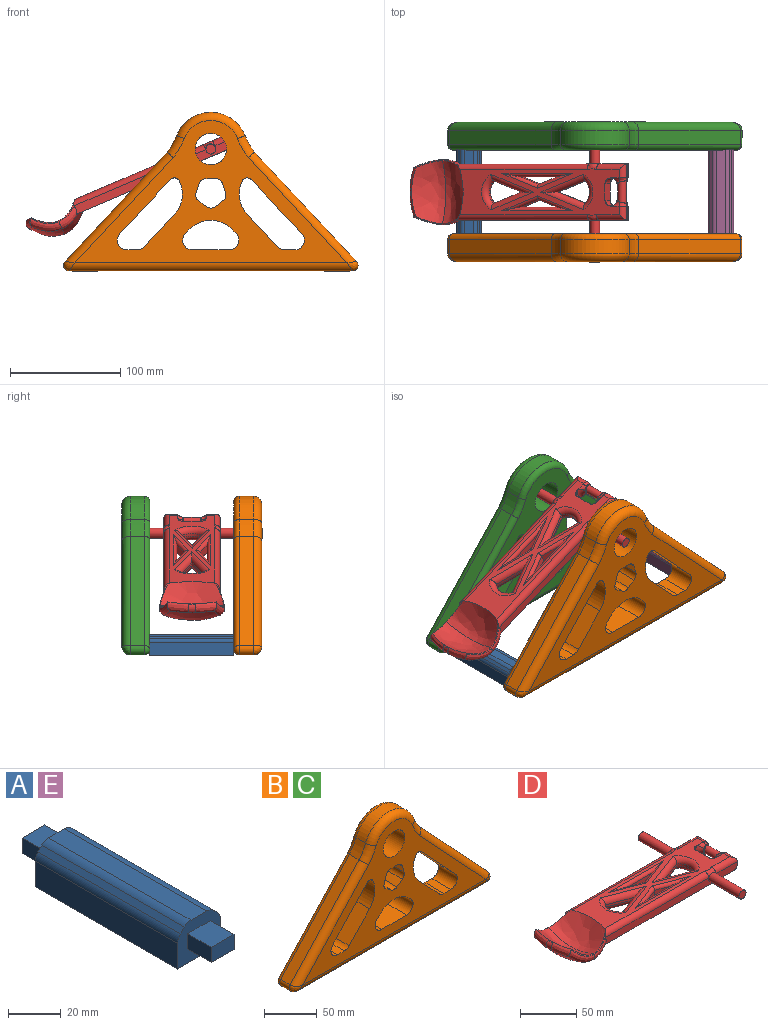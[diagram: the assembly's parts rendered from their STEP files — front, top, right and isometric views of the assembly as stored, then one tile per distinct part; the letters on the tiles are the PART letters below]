
ASSEMBLY  parts=5 mates=4
PART A: 22 faces, bbox 22.9x101.3x19.1 mm
  f0: plane 22.86x19.05mm, normal (0,-1,0), area 322.5mm2, adj f1,f2,f3,f4,f6,f7,f8,f9
  f1: plane 76.2x22.86mm, normal (0,0,-1), area 1741.9mm2, adj f0,f2,f4,f5
  f2: plane 76.2x11.87mm, normal (1,0,0), area 904.2mm2, adj f0,f1,f5,f8
  f3: plane 76.2x8.49mm, normal (0,0,1), area 647.1mm2, adj f0,f5,f9,f10
  f4: plane 76.2x11.87mm, normal (-1,0,0), area 904.2mm2, adj f0,f1,f5,f11
  f5: plane 22.86x19.05mm, normal (0,1,0), area 322.5mm2, adj f1,f2,f3,f4,f6,f7,f8,f9
  f6: plane 76.2x2.1mm, normal (-0.71,0,0.71), area 226.8mm2, adj f0,f5,f9,f11
  f7: plane 76.2x2.1mm, normal (0.71,0,0.71), area 226.8mm2, adj f0,f5,f8,f10
  f8: cylinder r=5.08mm len=76.2mm, axis (0,1,0), area 304mm2, adj f0,f2,f5,f7
  f9: cylinder r=5.08mm len=76.2mm, axis (0,1,0), area 304mm2, adj f0,f3,f5,f6
  f10: cylinder r=5.08mm len=76.2mm, axis (0,1,0), area 304mm2, adj f0,f3,f5,f7
  f11: cylinder r=5.08mm len=76.2mm, axis (0,-1,0), area 304mm2, adj f0,f4,f5,f6
  f12: plane 12.7x7.02mm, normal (1,0,0), area 89.2mm2, adj f0,f13,f15,f21
  f13: plane 12.7x12.1mm, normal (0,0,-1), area 153.7mm2, adj f0,f12,f14,f21
  f14: plane 12.7x7.02mm, normal (-1,0,0), area 89.2mm2, adj f0,f13,f15,f21
  f15: plane 12.7x12.1mm, normal (0,0,1), area 153.7mm2, adj f0,f12,f14,f21
  f16: plane 12.4x7.02mm, normal (1,0,0), area 87mm2, adj f5,f17,f19,f20
  f17: plane 12.1x7.02mm, normal (0,1,0), area 84.9mm2, adj f16,f18,f19,f20
  f18: plane 12.4x7.02mm, normal (-1,0,0), area 87mm2, adj f5,f17,f19,f20
  f19: plane 12.4x12.1mm, normal (0,0,1), area 150mm2, adj f5,f16,f17,f18
  f20: plane 12.4x12.1mm, normal (0,0,-1), area 150mm2, adj f5,f16,f17,f18
  f21: plane 12.1x7.02mm, normal (0,-1,0), area 84.9mm2, adj f12,f13,f14,f15
PART B: 67 faces, bbox 280x26.2x146.5 mm
  f0: plane 256.62x133.63mm, normal (0,1,0), area 11989.8mm2, adj f2,f3,f7,f8,f9,f10,f11,f12
  f1: plane 246.13x129.07mm, normal (0,-1,0), area 10767.5mm2, adj f2,f3,f7,f8,f9,f10,f11,f12
  f2: plane 25.4x9.31mm, normal (0,0,1), area 236.4mm2, adj f0,f1,f23,f25
  f3: cylinder r=14.29mm len=28.58mm, axis (0,1,0), area 2280.2mm2, adj f0,f1
  f4: plane 99.04x92.44mm, normal (0.73,0,0.68), area 1756mm2, adj f16,f37,f56,f57
  f5: plane 99.04x92.44mm, normal (-0.73,0,0.68), area 1756mm2, adj f17,f38,f49,f64
  f6: plane 256.62x12.96mm, normal (0,0,-1), area 3326.2mm2, adj f37,f38,f53,f60
  f7: plane 48.93x45.67mm, normal (-0.73,0,-0.68), area 1700.2mm2, adj f0,f1,f25,f65
  f8: plane 48.93x45.67mm, normal (0.73,0,-0.68), area 1700.2mm2, adj f0,f1,f26,f66
  f9: plane 25.4x9.31mm, normal (0,0,1), area 236.4mm2, adj f0,f1,f24,f26
  f10: plane 29.26x27.31mm, normal (0.73,0,0.68), area 1016.7mm2, adj f0,f1,f19,f23
  f11: plane 29.26x27.31mm, normal (-0.73,0,0.68), area 1016.7mm2, adj f0,f1,f20,f24
  f12: plane 25.4x3.54mm, normal (0.73,0,-0.68), area 123.1mm2, adj f0,f1,f18,f21
  f13: plane 33.42x25.4mm, normal (0,0,1), area 848.9mm2, adj f0,f1,f21,f22
  f14: plane 25.4x3.54mm, normal (-0.73,0,-0.68), area 123.1mm2, adj f0,f1,f18,f22
  f15: cylinder r=33.34mm len=62.04mm, axis (0,1,0), area 1033.4mm2, adj f16,f17,f52,f61
  f16: cylinder r=61.32mm len=15.07mm, axis (0,-1,0), area 225.4mm2, adj f4,f15,f54,f59
  f17: cylinder r=61.32mm len=15.07mm, axis (0,1,0), area 225.4mm2, adj f5,f15,f50,f63
  f18: cylinder r=27.09mm len=39.61mm, axis (0,1,0), area 1128.2mm2, adj f0,f1,f12,f14
  f19: cylinder r=27.09mm len=30.38mm, axis (0,1,0), area 829.5mm2, adj f0,f1,f10,f65
  f20: cylinder r=27.09mm len=30.38mm, axis (0,1,0), area 829.5mm2, adj f0,f1,f11,f66
  f21: cylinder r=8.75mm len=25.4mm, axis (0,-1,0), area 516.1mm2, adj f0,f1,f12,f13
  f22: cylinder r=8.75mm len=25.4mm, axis (0,-1,0), area 516.1mm2, adj f0,f1,f13,f14
  f23: cylinder r=8.75mm len=25.4mm, axis (0,-1,0), area 182.3mm2, adj f0,f1,f2,f10
  f24: cylinder r=8.75mm len=25.4mm, axis (0,1,0), area 182.3mm2, adj f0,f1,f9,f11
  f25: cylinder r=8.75mm len=25.4mm, axis (0,1,0), area 516.1mm2, adj f0,f1,f2,f7
  f26: cylinder r=8.75mm len=25.4mm, axis (0,1,0), area 516.1mm2, adj f0,f1,f8,f9
  f27: plane 25.4x7.21mm, normal (0.59,0,0.81), area 226.4mm2, adj f0,f1,f33,f34
  f28: plane 25.4x7.21mm, normal (-0.59,0,0.81), area 226.4mm2, adj f0,f1,f34,f36
  f29: plane 25.4x8.48mm, normal (-0.95,0,-0.31), area 226.4mm2, adj f0,f1,f35,f36
  f30: plane 25.4x8.91mm, normal (0,0,-1), area 226.4mm2, adj f0,f1,f32,f35
  f31: plane 25.4x8.48mm, normal (0.95,0,-0.31), area 226.4mm2, adj f0,f1,f32,f33
  f32: cylinder r=6.46mm len=25.4mm, axis (0,1,0), area 206.1mm2, adj f0,f1,f30,f31
  f33: cylinder r=6.46mm len=25.4mm, axis (0,1,0), area 206.1mm2, adj f0,f1,f27,f31
  f34: cylinder r=6.46mm len=25.4mm, axis (0,1,0), area 206.1mm2, adj f0,f1,f27,f28
  f35: cylinder r=6.46mm len=25.4mm, axis (0,1,0), area 206.1mm2, adj f0,f1,f29,f30
  f36: cylinder r=6.46mm len=25.4mm, axis (0,1,0), area 206.1mm2, adj f0,f1,f28,f29
  f37: cylinder r=5.08mm len=12.96mm, axis (0,-1,0), area 152.9mm2, adj f4,f6,f55,f58
  f38: cylinder r=5.08mm len=12.96mm, axis (0,-1,0), area 152.9mm2, adj f5,f6,f51,f62
  f39: plane 12.7x12.7mm, normal (0,0,-1), area 161.3mm2, adj f0,f40,f42,f43,f64
  f40: plane 12.7x7.62mm, normal (-1,0,0), area 96.8mm2, adj f0,f39,f41,f43
  f41: plane 12.7x12.7mm, normal (0,0,1), area 161.3mm2, adj f0,f40,f42,f43
  f42: plane 12.7x7.62mm, normal (1,0,0), area 96.8mm2, adj f0,f39,f41,f43,f64
  f43: plane 12.7x7.62mm, normal (0,1,0), area 96.8mm2, adj f39,f40,f41,f42
  f44: plane 12.7x7.62mm, normal (1,0,0), area 96.8mm2, adj f0,f45,f47,f48
  f45: plane 12.7x12.7mm, normal (0,0,-1), area 161.3mm2, adj f0,f44,f46,f48,f57
  f46: plane 12.7x7.62mm, normal (-1,0,0), area 96.8mm2, adj f0,f45,f47,f48,f57
  f47: plane 12.7x12.7mm, normal (0,0,1), area 161.3mm2, adj f0,f44,f46,f48
  f48: plane 12.7x7.62mm, normal (0,1,0), area 96.8mm2, adj f44,f45,f46,f47
  f49: cylinder r=7.36mm len=104.3mm, axis (0.68,0,0.73), area 1545.3mm2, adj f1,f5,f50,f51
  f50: torus R=68.68mm, axis (0,1,0), area 211.2mm2, adj f1,f17,f49,f52
  f51: bspline ~16.93x12.33mm, area 98mm2, adj f38,f49,f53
  f52: torus R=25.98mm, axis (0,1,0), area 847.7mm2, adj f1,f15,f50,f54
  f53: cylinder r=7.36mm len=256.62mm, axis (-1,0,0), area 2922.2mm2, adj f1,f6,f51,f55
  f54: torus R=68.68mm, axis (0,1,0), area 211.2mm2, adj f1,f16,f52,f56
  f55: bspline ~16.93x12.33mm, area 98mm2, adj f37,f53,f56
  f56: cylinder r=7.36mm len=104.3mm, axis (0.68,0,-0.73), area 1545.3mm2, adj f1,f4,f54,f55
  f57: cylinder r=5.08mm len=102.68mm, axis (-0.68,0,0.73), area 1081.7mm2, adj f0,f4,f45,f46,f58,f59
  f58: sphere r=5.08mm, area 59.9mm2, adj f37,f57,f60
  f59: torus R=66.4mm, axis (0,1,0), area 143.9mm2, adj f0,f16,f57,f61
  f60: cylinder r=5.08mm len=256.62mm, axis (1,0,0), area 2047.7mm2, adj f0,f6,f58,f62
  f61: torus R=28.26mm, axis (0,1,0), area 601mm2, adj f0,f15,f59,f63
  f62: sphere r=5.08mm, area 59.9mm2, adj f38,f60,f64
  f63: torus R=66.4mm, axis (0,1,0), area 143.9mm2, adj f0,f17,f61,f64
  f64: cylinder r=5.08mm len=102.68mm, axis (-0.68,0,-0.73), area 1081.7mm2, adj f0,f5,f39,f42,f62,f63
  f65: cylinder r=5.08mm len=25.4mm, axis (0,1,0), area 249.8mm2, adj f0,f1,f7,f19
  f66: cylinder r=5.08mm len=25.4mm, axis (0,1,0), area 249.8mm2, adj f0,f1,f8,f20
PART C: same geometry as B
PART D: 114 faces, bbox 228.8x139.9x39.4 mm
  f0: plane 3.94x1.57mm, normal (-1,0,0), area 2.5mm2, adj f1,f9,f14,f37,f113
  f1: cylinder r=5.08mm len=129.78mm, axis (-1,0,0), area 1022.9mm2, adj f0,f5,f9,f15,f28,f113
  f2: plane 36.48x6.57mm, normal (0,1,0), area 239.6mm2, adj f67,f68,f81,f90
  f3: plane 1.75x1.14mm, normal (0,-1,0), area 0.9mm2, adj f5,f48,f55
  f4: plane 1.75x1.14mm, normal (0,1,0), area 0.9mm2, adj f12,f41,f54
  f5: plane 157.9x44.26mm, normal (0,0,1), area 3253mm2, adj f1,f3,f15,f20,f21,f24,f25,f26
  f6: plane 13.08x2.92mm, normal (1,0,0), area 32.3mm2, adj f10,f22,f27,f45,f51
  f7: offset ~69.48x39.17mm, area 1089.9mm2, adj f12,f17,f31,f37
  f8: plane 41.67x14.21mm, normal (0,0.88,0.47), area 51.5mm2, adj f15,f16,f18,f31,f32,f33
  f9: plane 171.45x15.27mm, normal (0,-1,0), area 1220.4mm2, adj f0,f1,f11,f12,f23,f28,f29,f37
  f10: plane 171.45x15.27mm, normal (0,1,0), area 1220.4mm2, adj f6,f12,f18,f22,f24,f25,f26,f31
  f11: plane 13.08x2.92mm, normal (1,0,0), area 32.3mm2, adj f9,f23,f30,f38,f44
  f12: plane 175.09x63.68mm, normal (0,0,-1), area 4943.5mm2, adj f4,f7,f9,f10,f19,f21,f22,f23
  f13: cone r=41.27mm half-angle=33.7deg, axis (-1,0,0), area 3.4mm2, adj f33,f34,f35
  f14: plane 41.67x14.21mm, normal (0,-0.88,0.47), area 51.5mm2, adj f0,f15,f16,f35,f36,f37
  f15: bspline ~56.78x26.47mm, area 1620.2mm2, adj f1,f5,f8,f14,f16,f24,f112,f113
  f16: bspline ~56.78x26.47mm, area 1566.3mm2, adj f8,f14,f15,f33,f35
  f17: offset ~69.48x39.17mm, area 1534.5mm2, adj f7,f32,f33,f34,f35,f36
  f18: plane 3.94x1.57mm, normal (-1,0,0), area 2.5mm2, adj f8,f10,f24,f31,f112
  f19: plane 1.75x1.14mm, normal (0,-1,0), area 0.9mm2, adj f12,f48,f57
  f20: plane 1.75x1.14mm, normal (0,1,0), area 0.9mm2, adj f5,f41,f52
  f21: plane 15.49x12.7mm, normal (1,0,0), area 194.7mm2, adj f5,f12,f52,f53,f54,f55,f56,f57
  f22: cylinder r=5.08mm len=12.7mm, axis (0,1,0), area 101.3mm2, adj f6,f10,f12,f50
  f23: cylinder r=5.08mm len=12.7mm, axis (0,1,0), area 101.3mm2, adj f9,f11,f12,f43
  f24: cylinder r=5.08mm len=129.78mm, axis (1,0,0), area 1022.9mm2, adj f5,f10,f15,f18,f25,f112
  f25: bspline ~10.61x5.27mm, area 50.7mm2, adj f5,f10,f24,f26
  f26: cylinder r=5.08mm len=27.16mm, axis (1,0,0), area 196.5mm2, adj f5,f10,f25,f27
  f27: cylinder r=5.08mm len=12.7mm, axis (0,-1,0), area 81.1mm2, adj f5,f6,f26,f46
  f28: bspline ~10.61x5.27mm, area 50.7mm2, adj f1,f5,f9,f29
  f29: cylinder r=5.08mm len=27.16mm, axis (-1,0,0), area 196.5mm2, adj f5,f9,f28,f30
  f30: cylinder r=5.08mm len=12.7mm, axis (0,-1,0), area 81.1mm2, adj f5,f11,f29,f39
  f31: bspline ~27.95x15.74mm, area 166.3mm2, adj f7,f8,f10,f12,f18,f32
  f32: bspline ~34.17x21.98mm, area 241.4mm2, adj f8,f17,f31,f33
  f33: bspline ~29.07x10.69mm, area 179.5mm2, adj f8,f13,f16,f17,f32,f34
  f34: torus R=46.13mm, axis (-1,0,0), area 51.9mm2, adj f13,f17,f33,f35
  f35: bspline ~30.88x10.69mm, area 179.5mm2, adj f13,f14,f16,f17,f34,f36
  f36: bspline ~34.17x21.98mm, area 241.4mm2, adj f14,f17,f35,f37
  f37: bspline ~27.95x15.74mm, area 166.3mm2, adj f0,f7,f9,f12,f14,f36
  f38: bspline ~2.25x1.59mm, area 0.4mm2, adj f11,f39,f98
  f39: bspline ~6.12x5.09mm, area 22.5mm2, adj f30,f38,f40,f97
  f40: bspline ~8.34x5.27mm, area 27.5mm2, adj f5,f39,f41,f96
  f41: torus R=10.08mm, axis (0,1,0), area 74.5mm2, adj f4,f20,f40,f42,f53,f95
  f42: bspline ~8.36x5.31mm, area 27.5mm2, adj f12,f41,f43,f94
  f43: bspline ~6x5.46mm, area 22.4mm2, adj f23,f42,f44,f93
  f44: bspline ~2.45x1.72mm, area 0.4mm2, adj f11,f43,f106
  f45: bspline ~2.25x1.59mm, area 0.4mm2, adj f6,f46,f105
  f46: bspline ~6.12x5.09mm, area 22.5mm2, adj f27,f45,f47,f99
  f47: bspline ~8.34x5.27mm, area 27.5mm2, adj f5,f46,f48,f100
  f48: torus R=10.08mm, axis (0,1,0), area 74.5mm2, adj f3,f19,f47,f49,f56,f101
  f49: bspline ~8.36x5.31mm, area 27.5mm2, adj f12,f48,f50,f102
  f50: bspline ~6.01x5.08mm, area 22.4mm2, adj f22,f49,f51,f103
  f51: bspline ~2.45x1.72mm, area 0.4mm2, adj f6,f50,f104
  f52: cylinder r=5.08mm len=5.08mm, axis (0,0,1), area 14mm2, adj f5,f20,f21,f53
  f53: bspline ~10.08x5.32mm, area 66.5mm2, adj f21,f41,f52,f54
  f54: cylinder r=5.08mm len=5.08mm, axis (0,0,1), area 14mm2, adj f4,f12,f21,f53
  f55: cylinder r=5.08mm len=5.08mm, axis (0,0,-1), area 14mm2, adj f3,f5,f21,f56
  f56: bspline ~10.37x5.36mm, area 66.5mm2, adj f21,f48,f55,f57
  f57: cylinder r=5.08mm len=5.08mm, axis (0,0,-1), area 14mm2, adj f12,f19,f21,f56
  f58: cylinder r=13.76mm len=20.8mm, axis (0,0,1), area 59.9mm2, adj f61,f62,f69,f72
  f59: cylinder r=13.76mm len=20.8mm, axis (0,0,1), area 59.9mm2, adj f63,f64,f76,f79
  f60: plane 36.48x6.57mm, normal (0,-1,0), area 239.6mm2, adj f65,f66,f84,f87
  f61: plane 27.25x10.4mm, normal (-0.36,-0.93,0), area 74.1mm2, adj f58,f62,f70,f73
  f62: plane 27.25x10.4mm, normal (-0.36,0.93,0), area 74.1mm2, adj f58,f61,f71,f74
  f63: plane 27.25x10.4mm, normal (0.36,0.93,0), area 74.1mm2, adj f59,f64,f75,f78
  f64: plane 27.25x10.4mm, normal (0.36,-0.93,0), area 74.1mm2, adj f59,f63,f77,f80
  f65: plane 18.24x6.96mm, normal (0.36,0.93,0), area 128.2mm2, adj f60,f66,f86,f89
  f66: plane 18.24x6.96mm, normal (-0.36,0.93,0), area 128.2mm2, adj f60,f65,f85,f88
  f67: plane 18.24x6.96mm, normal (0.36,-0.93,0), area 128.2mm2, adj f2,f68,f83,f92
  f68: plane 18.24x6.96mm, normal (-0.36,-0.93,0), area 128.2mm2, adj f2,f67,f82,f91
  f69: torus R=18.84mm, axis (0,0,1), area 235.7mm2, adj f5,f58,f70,f71
  f70: cylinder r=5.08mm len=44.05mm, axis (0.93,-0.36,0), area 296.8mm2, adj f5,f61,f69,f71
  f71: cylinder r=5.08mm len=44.05mm, axis (0.93,0.36,0), area 296.8mm2, adj f5,f62,f69,f70
  f72: torus R=18.84mm, axis (0,0,1), area 235.7mm2, adj f12,f58,f73,f74
  f73: cylinder r=5.08mm len=44.05mm, axis (-0.93,0.36,0), area 296.8mm2, adj f12,f61,f72,f74
  f74: cylinder r=5.08mm len=44.05mm, axis (-0.93,-0.36,0), area 296.8mm2, adj f12,f62,f72,f73
  f75: cylinder r=5.08mm len=44.05mm, axis (0.93,-0.36,0), area 296.8mm2, adj f5,f63,f76,f77
  f76: torus R=18.84mm, axis (0,0,1), area 235.7mm2, adj f5,f59,f75,f77
  f77: cylinder r=5.08mm len=44.05mm, axis (0.93,0.36,0), area 296.8mm2, adj f5,f64,f75,f76
  f78: cylinder r=5.08mm len=44.05mm, axis (-0.93,0.36,0), area 296.8mm2, adj f12,f63,f79,f80
  f79: torus R=18.84mm, axis (0,0,1), area 235.7mm2, adj f12,f59,f78,f80
  f80: cylinder r=5.08mm len=44.05mm, axis (-0.93,-0.36,0), area 296.8mm2, adj f12,f64,f78,f79
  f81: cylinder r=3.07mm len=69.75mm, axis (-1,0,0), area 255.8mm2, adj f2,f5,f82,f83
  f82: cylinder r=3.07mm len=35.97mm, axis (-0.93,0.36,0), area 126mm2, adj f5,f68,f81,f83
  f83: cylinder r=3.07mm len=35.97mm, axis (0.93,0.36,0), area 126mm2, adj f5,f67,f81,f82
  f84: cylinder r=3.07mm len=69.75mm, axis (1,0,0), area 255.8mm2, adj f5,f60,f85,f86
  f85: cylinder r=3.07mm len=35.97mm, axis (0.93,0.36,0), area 126mm2, adj f5,f66,f84,f86
  f86: cylinder r=3.07mm len=35.97mm, axis (0.93,-0.36,0), area 126mm2, adj f5,f65,f84,f85
  f87: cylinder r=3.07mm len=69.75mm, axis (-1,0,0), area 255.8mm2, adj f12,f60,f88,f89
  f88: cylinder r=3.07mm len=35.97mm, axis (-0.93,-0.36,0), area 126mm2, adj f12,f66,f87,f89
  f89: cylinder r=3.07mm len=35.97mm, axis (-0.93,0.36,0), area 126mm2, adj f12,f65,f87,f88
  f90: cylinder r=3.07mm len=69.75mm, axis (1,0,0), area 255.8mm2, adj f2,f12,f91,f92
  f91: cylinder r=3.07mm len=35.97mm, axis (0.93,-0.36,0), area 126mm2, adj f12,f68,f90,f92
  f92: cylinder r=3.07mm len=35.97mm, axis (-0.93,-0.36,0), area 126mm2, adj f12,f67,f90,f91
  f93: bspline ~5x4.53mm, area 9mm2, adj f43,f94,f106,f107
  f94: bspline ~3.85x2.65mm, area 5.4mm2, adj f42,f93,f95,f107
  f95: plane 6.3x2.1mm, normal (0,1,0), area 7.6mm2, adj f41,f94,f96,f107
  f96: bspline ~3.85x2.65mm, area 5.4mm2, adj f40,f95,f97,f107
  f97: bspline ~5x4.53mm, area 9mm2, adj f39,f96,f98,f107
  f98: bspline ~1.3x0.9mm, area 1.3mm2, adj f38,f97,f106,f107
  f99: bspline ~5x4.53mm, area 9mm2, adj f46,f100,f105,f107
  f100: bspline ~3.85x2.65mm, area 5.4mm2, adj f47,f99,f101,f107
  f101: plane 6.3x2.1mm, normal (0,-1,0), area 7.6mm2, adj f48,f100,f102,f107
  f102: bspline ~3.85x2.65mm, area 5.4mm2, adj f49,f101,f103,f107
  f103: bspline ~5x4.53mm, area 9mm2, adj f50,f102,f104,f107
  f104: bspline ~1.3x0.9mm, area 1.3mm2, adj f51,f103,f105,f107
  f105: bspline ~1.3x0.9mm, area 1.3mm2, adj f45,f99,f104,f107
  f106: bspline ~1.3x0.9mm, area 1.3mm2, adj f44,f93,f98,f107
  f107: cylinder r=3.73mm len=25.4mm, axis (0,-1,0), area 427.7mm2, adj f93,f94,f95,f96,f97,f98,f99,f100
  f108: cylinder r=4.46mm len=38.1mm, axis (0,1,0), area 1068.3mm2, adj f10,f110
  f109: cylinder r=4.46mm len=38.1mm, axis (0,1,0), area 1068.3mm2, adj f9,f111
  f110: plane 8.93x8.93mm, normal (0,1,0), area 62.6mm2, adj f108
  f111: plane 8.93x8.93mm, normal (0,-1,0), area 62.6mm2, adj f109
  f112: extruded ~3.68x3.06mm, area 2.7mm2, adj f15,f18,f24
  f113: extruded ~3.68x3.06mm, area 2.7mm2, adj f0,f1,f15
PART E: same geometry as A
PLACE A t=(-183.55,-13.21,39.08)mm
PLACE B t=(-69.25,-102.11,29.56)mm fixed
PLACE C rot(axis=(0,0,1),180deg) t=(-69.25,-26.21,29.56)mm
PLACE D rot(axis=(0,-1,0),23.1deg) t=(-116.4,-64.31,112.99)mm
PLACE E t=(45.05,-13.21,39.08)mm
MATE fastened A.f17 <-> C.f48  axis (0,1,0) through (-183.55,-13.51,39.08)mm
MATE fastened A.f21 <-> B.f43  axis (0,-1,0) through (-183.55,-114.81,39.08)mm
MATE fastened E.f21 <-> B.f48  axis (0,-1,0) through (45.05,-114.81,39.08)mm
MATE revolute D.f108 <-> C.f3  axis (0,1,0) through (-69.25,-0.81,140.01)mm
